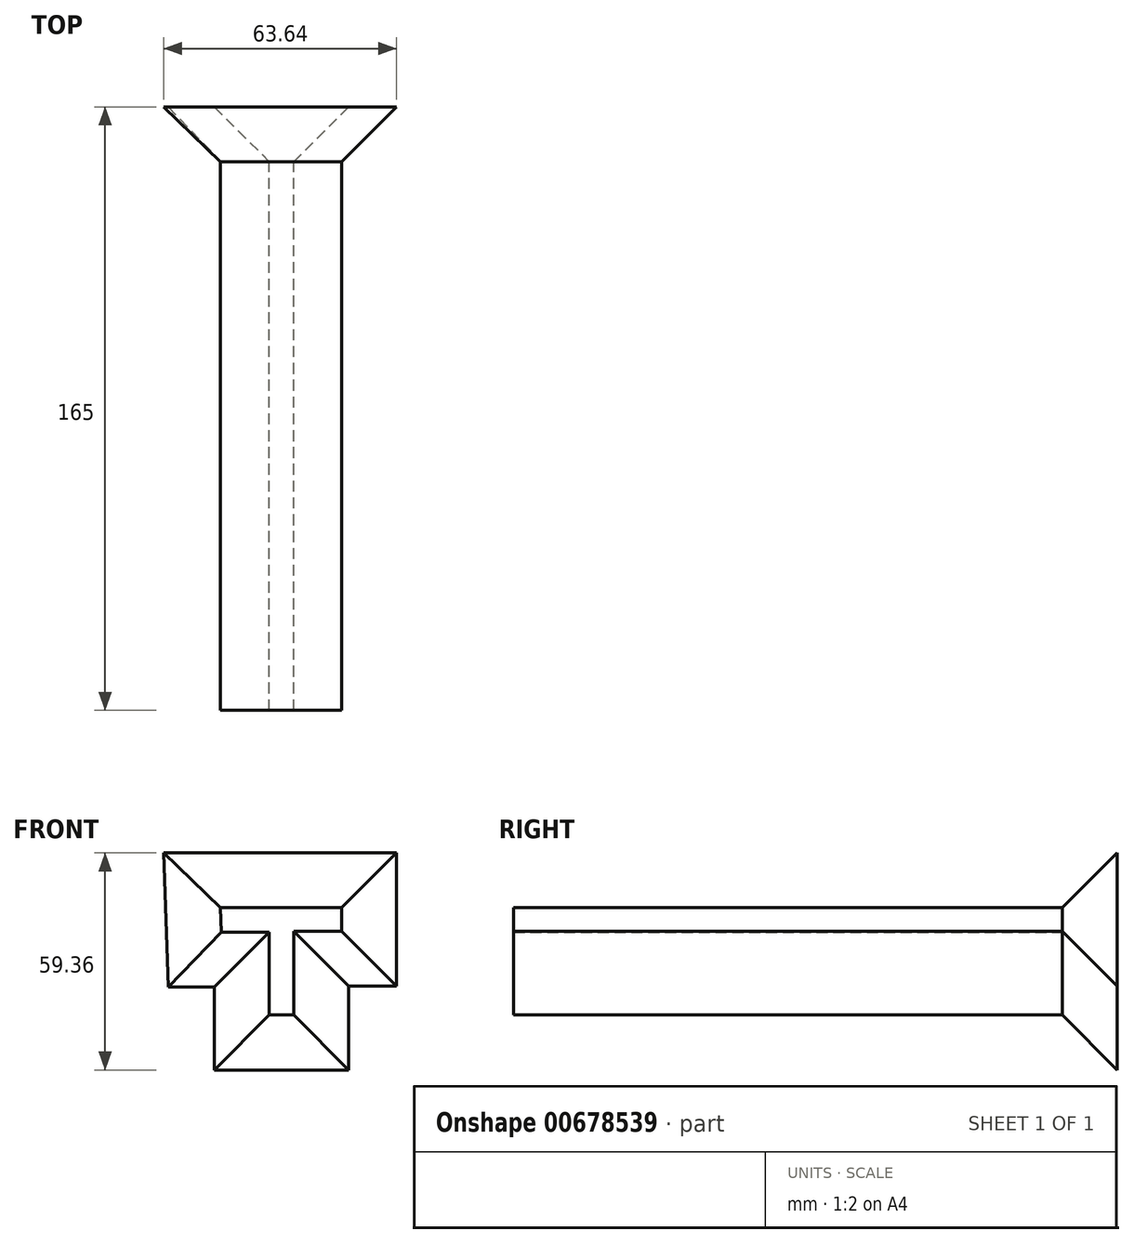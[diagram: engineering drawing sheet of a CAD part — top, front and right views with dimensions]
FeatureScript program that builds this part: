
annotation { "Feature Type Name" : "Feature", "Feature Type Description" : "" }
export const myFeature = defineFeature(function(context is Context, id is Id, definition is map)
    precondition{}
    {
        {
            var Q0;
            Q0=qCreatedBy(makeId("Front.planeOp"),FACE);
            var sketch = newSketch(context, id + "F0", { "sketchPlane" : qUnion([Q0])});
            skLineSegment(sketch, "E0", {"start": v(-16.66, 10.63) * mm, "end": v(16.48, 10.63) * mm});
            skLineSegment(sketch, "E1", {"start": v(16.48, 10.63) * mm, "end": v(16.48, 4.16) * mm});
            skLineSegment(sketch, "E2", {"start": v(16.48, 4.16) * mm, "end": v(3.38, 4.16) * mm});
            skLineSegment(sketch, "E3", {"start": v(3.38, 4.16) * mm, "end": v(3.38, -18.73) * mm});
            skLineSegment(sketch, "E4", {"start": v(3.38, -18.73) * mm, "end": v(-3.3, -18.73) * mm});
            skLineSegment(sketch, "E5", {"start": v(-3.3, -18.73) * mm, "end": v(-3.3, 3.94) * mm});
            skLineSegment(sketch, "E6", {"start": v(-3.3, 3.94) * mm, "end": v(-16.44, 3.94) * mm});
            skLineSegment(sketch, "E7", {"start": v(-16.44, 3.94) * mm, "end": v(-16.66, 10.63) * mm});
            skSolve(sketch);
        }
        {
            var Q0;
            Q0=makeQuery(id+"F0.imprint","IMPRINT",FACE,{"disambiguationData":[TD([[makeQuery(id+"F0.imprint","IMPRINT",EDGE,{"derivedFrom":sQuery(id+"F0.wireOp",EDGE,"E0")}),-1.0]])]});
            extrude(context, id + "F1", {"entities" : qUnion([Q0]), "depth" : 150 * mm, "offsetDistance" : 25 * mm});
        }
        {
            var Q0;
            Q0=makeQuery(id+"F1.opExtrude","CAP_FACE",FACE,{"disambiguationData":[OSD([sQuery(id+"F0.wireOp",EDGE,"E0"),sQuery(id+"F0.wireOp",EDGE,"E1"),sQuery(id+"F0.wireOp",EDGE,"E2"),sQuery(id+"F0.wireOp",EDGE,"E3"),sQuery(id+"F0.wireOp",EDGE,"E4"),sQuery(id+"F0.wireOp",EDGE,"E5"),sQuery(id+"F0.wireOp",EDGE,"E6"),sQuery(id+"F0.wireOp",EDGE,"E7")])],"isStart":true});
            var sketch = newSketch(context, id + "F2", { "sketchPlane" : qUnion([Q0])});
            skCircle(sketch, "E8", {"center": v(0, 0) * mm, "radius": 19.76 * mm});
            skSolve(sketch);
        }
        {
            var Q0;
            Q0=makeQuery(id+"F2.imprint","IMPRINT",FACE,{"disambiguationData":[TD([[makeQuery(id+"F2.imprint","IMPRINT",EDGE,{"derivedFrom":makeQuery(id+"F1.opExtrude","CAP_EDGE",EDGE,{"disambiguationData":[OSD([sQuery(id+"F0.wireOp",EDGE,"E0")])],"isStart":true})}),1.0]])]});
            extrude(context, id + "F3", {"entities" : qUnion([Q0]), "operationType" : NewBodyOperationType.ADD, "depth" : 15 * mm, "offsetDistance" : 25 * mm, "hasDraft" : true, "draftAngle" : 45 * degree});
        }
    });
